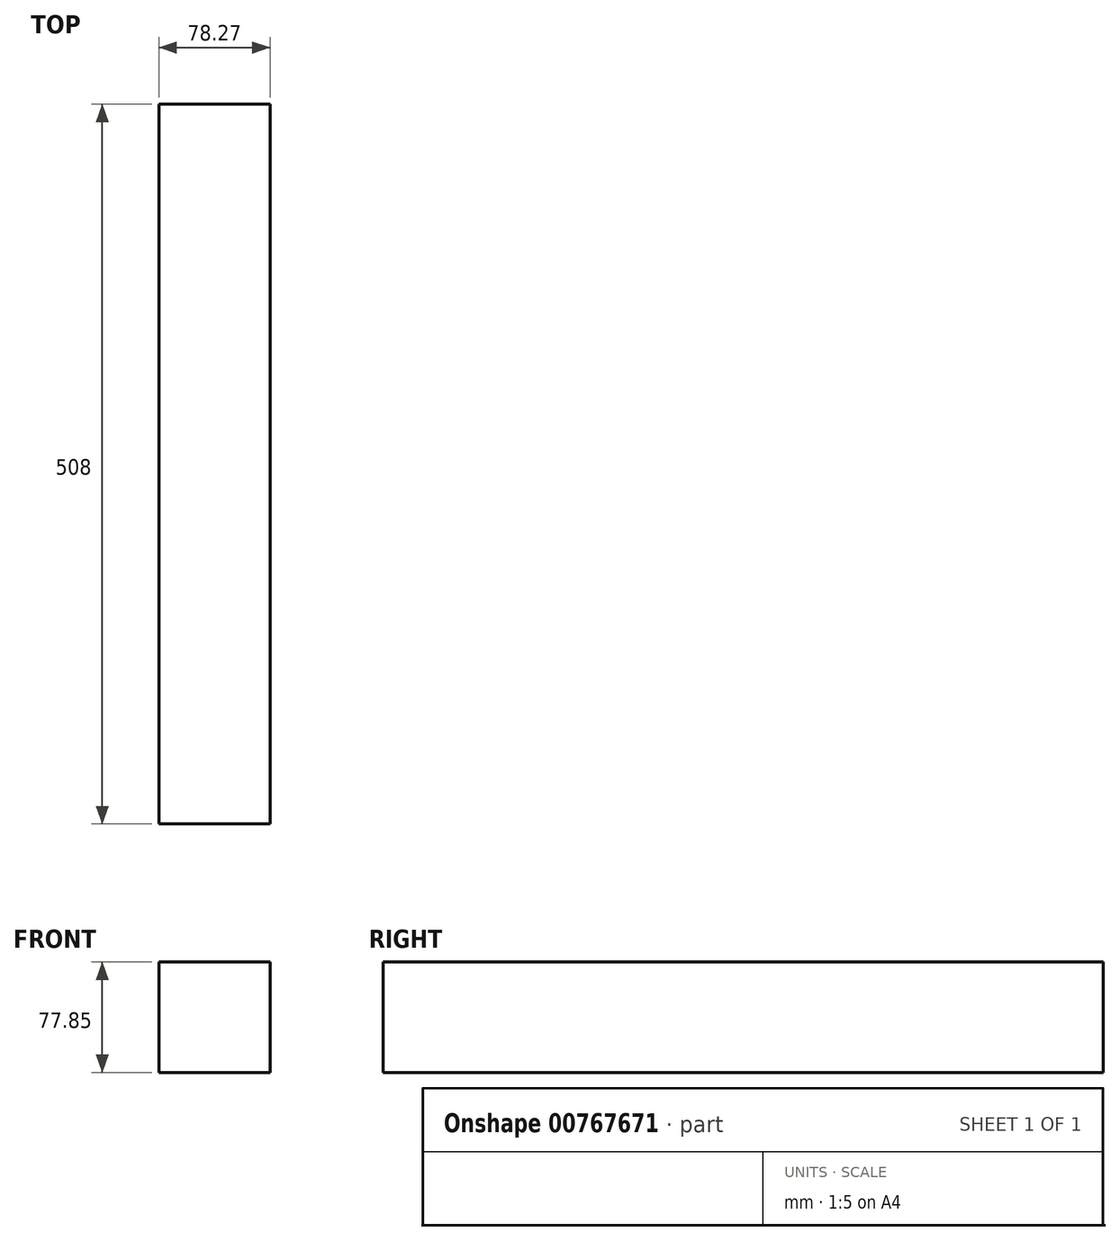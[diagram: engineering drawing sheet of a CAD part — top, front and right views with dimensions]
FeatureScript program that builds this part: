
annotation { "Feature Type Name" : "Feature", "Feature Type Description" : "" }
export const myFeature = defineFeature(function(context is Context, id is Id, definition is map)
    precondition{}
    {
        {
            var Q0;
            Q0=qCreatedBy(makeId("Front.planeOp"),FACE);
            var sketch = newSketch(context, id + "F0", { "sketchPlane" : qUnion([Q0])});
            skCircle(sketch, "E0", {"center": v(0, 0) * mm, "radius": 13.83 * mm});
            skLineSegment(sketch, "E1", {"start": v(-5.88, -12.52) * mm, "end": v(-5.88, -29.03) * mm});
            skLineSegment(sketch, "E2", {"start": v(-5.88, -29.03) * mm, "end": v(5.26, -29.03) * mm});
            skLineSegment(sketch, "E3", {"start": v(5.26, -29.03) * mm, "end": v(5.26, -12.8) * mm});
            skSolve(sketch);
        }
        {
            var Q0;
            {var subQ0=sQuery(id+"F0.wireOp",EDGE,"E0");var subQ1=makeQuery(id+"F0.imprint","INTERSECT",VERTEX,{"derivedFrom":[subQ0,sQuery(id+"F0.wireOp",EDGE,"E1")]});Q0=makeQuery(id+"F0.imprint","IMPRINT",FACE,{"disambiguationData":[TD([[makeQuery(id+"F0.imprint","IMPRINT",EDGE,{"disambiguationData":[TD([[subQ1,-1.0]])],"derivedFrom":subQ0}),1.0]])]});}
            var Q1;
            {var subQ0=sQuery(id+"F0.wireOp",EDGE,"E1");Q1=makeQuery(id+"F0.imprint","IMPRINT",FACE,{"disambiguationData":[TD([[makeQuery(id+"F0.imprint","IMPRINT",EDGE,{"derivedFrom":subQ0}),1.0]])]});}
            extrude(context, id + "F1", {"entities" : qUnion([Q0, Q1]), "oppositeDirection" : true, "depth" : 127 * mm, "offsetDistance" : 25.4 * mm});
        }
        {
            var Q0;
            Q0=makeQuery(id+"F1.opExtrude","CAP_EDGE",EDGE,{"disambiguationData":[OSD([sQuery(id+"F0.wireOp",EDGE,"E1")])],"isStart":true});
            var Q1;
            Q1=makeQuery(id+"F1.opExtrude","CAP_EDGE",EDGE,{"disambiguationData":[OSD([sQuery(id+"F0.wireOp",EDGE,"E3")])],"isStart":true});
            fillet(context, id + "F2", {"entities" : qUnion([Q0, Q1]), "radius" : 5.08 * mm, "tangentPropagation" : true, "allowEdgeOverflow" : false});
        }
        {
            var Q0;
            Q0=makeQuery(id+"F1.opExtrude","CAP_EDGE",EDGE,{"disambiguationData":[OSD([sQuery(id+"F0.wireOp",EDGE,"E0")])],"isStart":true});
            fillet(context, id + "F3", {"entities" : qUnion([Q0]), "radius" : 5.08 * mm, "tangentPropagation" : true, "allowEdgeOverflow" : false});
        }
        {
            var Q0;
            {var subQ0=sQuery(id+"F0.wireOp",EDGE,"E0");Q0=makeQuery(id+"F3.opFillet","BLEND_EDGE",EDGE,{"blendedFrom":[makeQuery(id+"F1.opExtrude","CAP_EDGE",EDGE,{"disambiguationData":[OSD([subQ0])],"isStart":true}),makeQuery(id+"F1.opExtrude","CAP_FACE",FACE,{"disambiguationData":[OSD([subQ0,sQuery(id+"F0.wireOp",EDGE,"E1"),sQuery(id+"F0.wireOp",EDGE,"E2"),sQuery(id+"F0.wireOp",EDGE,"E3")])],"isStart":true})],"blendedInto":[makeQuery(id+"F1.opExtrude","CAP_FACE",FACE,{"disambiguationData":[OSD([subQ0,sQuery(id+"F0.wireOp",EDGE,"E1"),sQuery(id+"F0.wireOp",EDGE,"E2"),sQuery(id+"F0.wireOp",EDGE,"E3")])],"isStart":true})]});}
            var Q1;
            Q1=makeQuery(id+"F2.opFillet","BLEND_FACE",FACE,{"disambiguationData":[OSD([sQuery(id+"F0.wireOp",EDGE,"E3")])]});
            var Q2;
            {var subQ0=sQuery(id+"F0.wireOp",EDGE,"E0");Q2=makeQuery(id+"F3.opFillet","BLEND_EDGE",EDGE,{"blendedFrom":[makeQuery(id+"F1.opExtrude","CAP_EDGE",EDGE,{"disambiguationData":[OSD([subQ0])],"isStart":true}),makeQuery(id+"F1.opExtrude","SWEPT_FACE",FACE,{"disambiguationData":[OSD([subQ0])]})],"blendedInto":[makeQuery(id+"F1.opExtrude","SWEPT_FACE",FACE,{"disambiguationData":[OSD([subQ0])]})]});}
            var Q3;
            Q3=makeQuery(id+"F1.opExtrude","SWEPT_EDGE",EDGE,{"disambiguationData":[OSD([sQuery(id+"F0.wireOp",EDGE,"E0"),sQuery(id+"F0.wireOp",EDGE,"E3")])]});
            var Q4;
            Q4=makeQuery(id+"F1.opExtrude","SWEPT_FACE",FACE,{"disambiguationData":[OSD([sQuery(id+"F0.wireOp",EDGE,"E0")])]});
            chamfer(context, id + "F4", {"entities" : qUnion([Q0, Q1, Q2, Q3, Q4]), "width" : 5.08 * mm, "tangentPropagation" : true});
        }
        {
            var Q0;
            Q0=qCreatedBy(makeId("Front.planeOp"),FACE);
            var sketch = newSketch(context, id + "F5", { "sketchPlane" : qUnion([Q0])});
            skLineSegment(sketch, "E4.bottom", {"start": v(-36.63, 29.79) * mm, "end": v(41.64, 29.79) * mm});
            skLineSegment(sketch, "E4.top", {"start": v(-36.63, -48.06) * mm, "end": v(41.64, -48.06) * mm});
            skLineSegment(sketch, "E4.left", {"start": v(-36.63, 29.79) * mm, "end": v(-36.63, -48.06) * mm});
            skLineSegment(sketch, "E4.right", {"start": v(41.64, 29.79) * mm, "end": v(41.64, -48.06) * mm});
            skSolve(sketch);
        }
        {
            var Q0;
            Q0=makeQuery(id+"F5.imprint","IMPRINT",FACE,{"disambiguationData":[TD([[makeQuery(id+"F5.imprint","IMPRINT",EDGE,{"derivedFrom":sQuery(id+"F5.wireOp",EDGE,"E4.bottom")}),-1.0]])]});
            extrude(context, id + "F6", {"entities" : qUnion([Q0]), "operationType" : NewBodyOperationType.ADD, "endBound" : BoundingType.SYMMETRIC, "depth" : 508 * mm, "offsetDistance" : 25.4 * mm});
        }
    });
